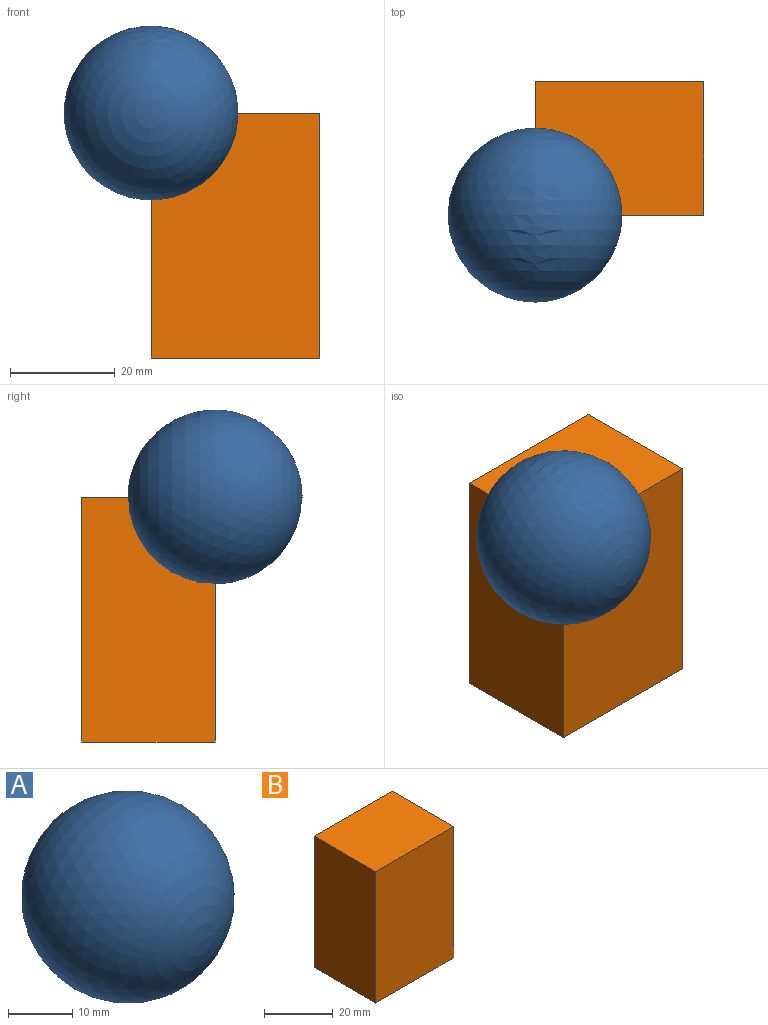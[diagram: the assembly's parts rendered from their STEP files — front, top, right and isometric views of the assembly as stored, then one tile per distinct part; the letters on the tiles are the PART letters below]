
ASSEMBLY  parts=2 mates=1
PART A: 1 faces, bbox 33.2x33.2x33.2 mm
  f0: sphere r=16.6mm, area 3461.1mm2
PART B: 6 faces, bbox 32.1x25.4x46.7 mm
  f0: plane 32.15x25.4mm, normal (0,0,1), area 816.6mm2, adj f1,f3,f4,f5
  f1: plane 46.72x25.4mm, normal (-1,0,0), area 1186.7mm2, adj f0,f2,f4,f5
  f2: plane 32.15x25.4mm, normal (0,0,-1), area 816.6mm2, adj f1,f3,f4,f5
  f3: plane 46.72x25.4mm, normal (1,0,0), area 1186.7mm2, adj f0,f2,f4,f5
  f4: plane 46.72x32.15mm, normal (0,-1,0), area 1502mm2, adj f0,f1,f2,f3
  f5: plane 46.72x32.15mm, normal (0,1,0), area 1502mm2, adj f0,f1,f2,f3
PLACE A rot(axis=(0,-1,0),90deg) t=(-51.17,11.49,45.1)mm
PLACE B t=(18.48,6.93,5.23)mm
MATE planar A.f0 <-> B.f1  axis (-1,0,0) through (-51.17,-18.47,45.1)mm
